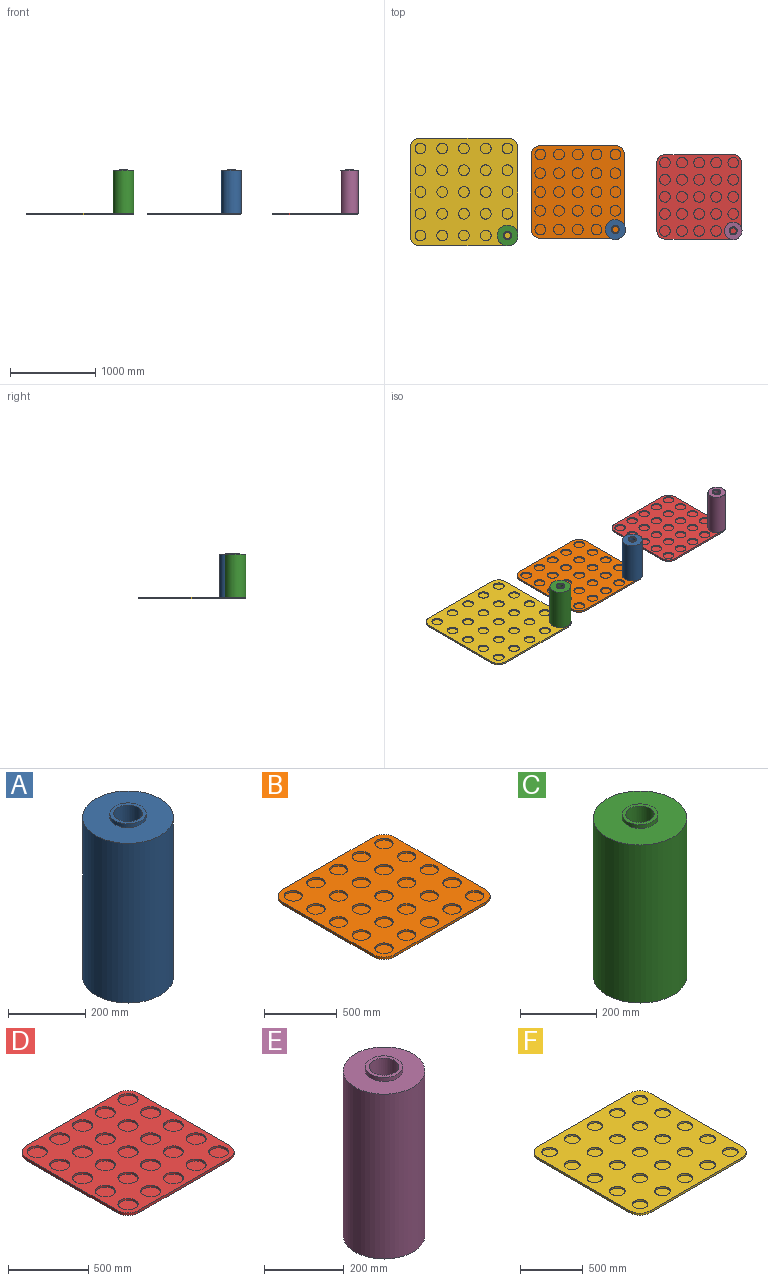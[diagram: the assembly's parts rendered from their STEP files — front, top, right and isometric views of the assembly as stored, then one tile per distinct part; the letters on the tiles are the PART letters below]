
ASSEMBLY  parts=6 mates=8
PART A: 8 faces, bbox 235x235x530 mm
  f0: cylinder r=117.5mm len=506mm, axis (0,0,-1), area 373566.8mm2, adj f3,f7
  f1: plane 94x94mm, normal (0,0,-1), area 2638.9mm2, adj f5,f6
  f2: cylinder r=47mm len=94mm, axis (0,0,1), area 3543.7mm2, adj f3,f4
  f3: plane 235x235mm, normal (0,0,1), area 36433.8mm2, adj f0,f2
  f4: plane 94x94mm, normal (0,0,1), area 2638.9mm2, adj f2,f5
  f5: cylinder r=37mm len=530mm, axis (0,0,1), area 123213.3mm2, adj f1,f4
  f6: cylinder r=47mm len=94mm, axis (0,0,-1), area 3543.7mm2, adj f1,f7
  f7: plane 235x235mm, normal (0,0,-1), area 36433.8mm2, adj f0,f6
PART B: 60 faces, bbox 1090x1090x20 mm
  f0: plane 1090x1090mm, normal (0,0,1), area 871839.9mm2, adj f1,f2,f3,f4,f5,f6,f7,f8
  f1: plane 880x20mm, normal (1,0,0), area 17600mm2, adj f0,f2,f8,f9
  f2: cylinder r=105mm len=105mm, axis (0,0,-1), area 3298.7mm2, adj f0,f1,f3,f9
  f3: plane 880x20mm, normal (0,1,0), area 17600mm2, adj f0,f2,f4,f9
  f4: cylinder r=105mm len=105mm, axis (0,0,-1), area 3298.7mm2, adj f0,f3,f5,f9
  f5: plane 880x20mm, normal (-1,0,0), area 17600mm2, adj f0,f4,f6,f9
  f6: cylinder r=105mm len=105mm, axis (0,0,-1), area 3298.7mm2, adj f0,f5,f7,f9
  f7: plane 880x20mm, normal (0,-1,0), area 17600mm2, adj f0,f6,f8,f9
  f8: cylinder r=105mm len=105mm, axis (0,0,-1), area 3298.7mm2, adj f0,f1,f7,f9
  f9: plane 1090x1090mm, normal (0,0,-1), area 1178636.1mm2, adj f1,f2,f3,f4,f5,f6,f7,f8
  f10: cylinder r=62.5mm len=125mm, axis (0,0,1), area 5890.5mm2, adj f0,f11
  f11: plane 125x125mm, normal (0,0,1), area 12271.8mm2, adj f10
  f12: cylinder r=62.5mm len=125mm, axis (0,0,1), area 5890.5mm2, adj f0,f13
  f13: plane 125x125mm, normal (0,0,1), area 12271.8mm2, adj f12
  f14: cylinder r=62.5mm len=125mm, axis (0,0,1), area 5890.5mm2, adj f0,f15
  f15: plane 125x125mm, normal (0,0,1), area 12271.8mm2, adj f14
  f16: cylinder r=62.5mm len=125mm, axis (0,0,1), area 5890.5mm2, adj f0,f17
  f17: plane 125x125mm, normal (0,0,1), area 12271.8mm2, adj f16
  f18: cylinder r=62.5mm len=125mm, axis (0,0,1), area 5890.5mm2, adj f0,f19
  f19: plane 125x125mm, normal (0,0,1), area 12271.8mm2, adj f18
  f20: cylinder r=62.5mm len=125mm, axis (0,0,1), area 5890.5mm2, adj f0,f21
  f21: plane 125x125mm, normal (0,0,1), area 12271.8mm2, adj f20
  f22: cylinder r=62.5mm len=125mm, axis (0,0,1), area 5890.5mm2, adj f0,f23
  f23: plane 125x125mm, normal (0,0,1), area 12271.8mm2, adj f22
  f24: cylinder r=62.5mm len=125mm, axis (0,0,1), area 5890.5mm2, adj f0,f25
  f25: plane 125x125mm, normal (0,0,1), area 12271.8mm2, adj f24
  f26: cylinder r=62.5mm len=125mm, axis (0,0,1), area 5890.5mm2, adj f0,f27
  f27: plane 125x125mm, normal (0,0,1), area 12271.8mm2, adj f26
  f28: cylinder r=62.5mm len=125mm, axis (0,0,1), area 5890.5mm2, adj f0,f29
  f29: plane 125x125mm, normal (0,0,1), area 12271.8mm2, adj f28
  f30: cylinder r=62.5mm len=125mm, axis (0,0,1), area 5890.5mm2, adj f0,f31
  f31: plane 125x125mm, normal (0,0,1), area 12271.8mm2, adj f30
  f32: cylinder r=62.5mm len=125mm, axis (0,0,1), area 5890.5mm2, adj f0,f33
  f33: plane 125x125mm, normal (0,0,1), area 12271.8mm2, adj f32
  f34: cylinder r=62.5mm len=125mm, axis (0,0,1), area 5890.5mm2, adj f0,f35
  f35: plane 125x125mm, normal (0,0,1), area 12271.8mm2, adj f34
  f36: cylinder r=62.5mm len=125mm, axis (0,0,1), area 5890.5mm2, adj f0,f37
  f37: plane 125x125mm, normal (0,0,1), area 12271.8mm2, adj f36
  f38: cylinder r=62.5mm len=125mm, axis (0,0,1), area 5890.5mm2, adj f0,f39
  f39: plane 125x125mm, normal (0,0,1), area 12271.8mm2, adj f38
  f40: cylinder r=62.5mm len=125mm, axis (0,0,1), area 5890.5mm2, adj f0,f41
  f41: plane 125x125mm, normal (0,0,1), area 12271.8mm2, adj f40
  f42: cylinder r=62.5mm len=125mm, axis (0,0,1), area 5890.5mm2, adj f0,f43
  f43: plane 125x125mm, normal (0,0,1), area 12271.8mm2, adj f42
  f44: cylinder r=62.5mm len=125mm, axis (0,0,1), area 5890.5mm2, adj f0,f45
  f45: plane 125x125mm, normal (0,0,1), area 12271.8mm2, adj f44
  f46: cylinder r=62.5mm len=125mm, axis (0,0,1), area 5890.5mm2, adj f0,f47
  f47: plane 125x125mm, normal (0,0,1), area 12271.8mm2, adj f46
  f48: cylinder r=62.5mm len=125mm, axis (0,0,1), area 5890.5mm2, adj f0,f49
  f49: plane 125x125mm, normal (0,0,1), area 12271.8mm2, adj f48
  f50: cylinder r=62.5mm len=125mm, axis (0,0,1), area 5890.5mm2, adj f0,f51
  f51: plane 125x125mm, normal (0,0,1), area 12271.8mm2, adj f50
  f52: cylinder r=62.5mm len=125mm, axis (0,0,1), area 5890.5mm2, adj f0,f53
  f53: plane 125x125mm, normal (0,0,1), area 12271.8mm2, adj f52
  f54: cylinder r=62.5mm len=125mm, axis (0,0,1), area 5890.5mm2, adj f0,f55
  f55: plane 125x125mm, normal (0,0,1), area 12271.8mm2, adj f54
  f56: cylinder r=62.5mm len=125mm, axis (0,0,1), area 5890.5mm2, adj f0,f57
  f57: plane 125x125mm, normal (0,0,1), area 12271.8mm2, adj f56
  f58: cylinder r=62.5mm len=125mm, axis (0,0,1), area 5890.5mm2, adj f0,f59
  f59: plane 125x125mm, normal (0,0,1), area 12271.8mm2, adj f58
PART C: 8 faces, bbox 245x245x530 mm
  f0: cylinder r=122.5mm len=506mm, axis (0,0,-1), area 389463.2mm2, adj f3,f7
  f1: plane 94x94mm, normal (0,0,-1), area 2638.9mm2, adj f5,f6
  f2: cylinder r=47mm len=94mm, axis (0,0,1), area 3543.7mm2, adj f3,f4
  f3: plane 245x245mm, normal (0,0,1), area 40203.7mm2, adj f0,f2
  f4: plane 94x94mm, normal (0,0,1), area 2638.9mm2, adj f2,f5
  f5: cylinder r=37mm len=530mm, axis (0,0,1), area 123213.3mm2, adj f1,f4
  f6: cylinder r=47mm len=94mm, axis (0,0,-1), area 3543.7mm2, adj f1,f7
  f7: plane 245x245mm, normal (0,0,-1), area 40203.7mm2, adj f0,f6
PART D: 60 faces, bbox 990x990x20 mm
  f0: plane 990x990mm, normal (0,0,1), area 665556.7mm2, adj f1,f2,f3,f4,f5,f6,f7,f8
  f1: plane 800x20mm, normal (1,0,0), area 16000mm2, adj f0,f2,f8,f9
  f2: cylinder r=95mm len=95mm, axis (0,0,-1), area 2984.5mm2, adj f0,f1,f3,f9
  f3: plane 800x20mm, normal (0,1,0), area 16000mm2, adj f0,f2,f4,f9
  f4: cylinder r=95mm len=95mm, axis (0,0,-1), area 2984.5mm2, adj f0,f3,f5,f9
  f5: plane 800x20mm, normal (-1,0,0), area 16000mm2, adj f0,f4,f6,f9
  f6: cylinder r=95mm len=95mm, axis (0,0,-1), area 2984.5mm2, adj f0,f5,f7,f9
  f7: plane 800x20mm, normal (0,-1,0), area 16000mm2, adj f0,f6,f8,f9
  f8: cylinder r=95mm len=95mm, axis (0,0,-1), area 2984.5mm2, adj f0,f1,f7,f9
  f9: plane 990x990mm, normal (0,0,-1), area 972352.9mm2, adj f1,f2,f3,f4,f5,f6,f7,f8
  f10: cylinder r=62.5mm len=125mm, axis (0,0,1), area 5890.5mm2, adj f0,f11
  f11: plane 125x125mm, normal (0,0,1), area 12271.8mm2, adj f10
  f12: cylinder r=62.5mm len=125mm, axis (0,0,1), area 5890.5mm2, adj f0,f13
  f13: plane 125x125mm, normal (0,0,1), area 12271.8mm2, adj f12
  f14: cylinder r=62.5mm len=125mm, axis (0,0,1), area 5890.5mm2, adj f0,f15
  f15: plane 125x125mm, normal (0,0,1), area 12271.8mm2, adj f14
  f16: cylinder r=62.5mm len=125mm, axis (0,0,1), area 5890.5mm2, adj f0,f17
  f17: plane 125x125mm, normal (0,0,1), area 12271.8mm2, adj f16
  f18: cylinder r=62.5mm len=125mm, axis (0,0,1), area 5890.5mm2, adj f0,f19
  f19: plane 125x125mm, normal (0,0,1), area 12271.8mm2, adj f18
  f20: cylinder r=62.5mm len=125mm, axis (0,0,1), area 5890.5mm2, adj f0,f21
  f21: plane 125x125mm, normal (0,0,1), area 12271.8mm2, adj f20
  f22: cylinder r=62.5mm len=125mm, axis (0,0,1), area 5890.5mm2, adj f0,f23
  f23: plane 125x125mm, normal (0,0,1), area 12271.8mm2, adj f22
  f24: cylinder r=62.5mm len=125mm, axis (0,0,1), area 5890.5mm2, adj f0,f25
  f25: plane 125x125mm, normal (0,0,1), area 12271.8mm2, adj f24
  f26: cylinder r=62.5mm len=125mm, axis (0,0,1), area 5890.5mm2, adj f0,f27
  f27: plane 125x125mm, normal (0,0,1), area 12271.8mm2, adj f26
  f28: cylinder r=62.5mm len=125mm, axis (0,0,1), area 5890.5mm2, adj f0,f29
  f29: plane 125x125mm, normal (0,0,1), area 12271.8mm2, adj f28
  f30: cylinder r=62.5mm len=125mm, axis (0,0,1), area 5890.5mm2, adj f0,f31
  f31: plane 125x125mm, normal (0,0,1), area 12271.8mm2, adj f30
  f32: cylinder r=62.5mm len=125mm, axis (0,0,1), area 5890.5mm2, adj f0,f33
  f33: plane 125x125mm, normal (0,0,1), area 12271.8mm2, adj f32
  f34: cylinder r=62.5mm len=125mm, axis (0,0,1), area 5890.5mm2, adj f0,f35
  f35: plane 125x125mm, normal (0,0,1), area 12271.8mm2, adj f34
  f36: cylinder r=62.5mm len=125mm, axis (0,0,1), area 5890.5mm2, adj f0,f37
  f37: plane 125x125mm, normal (0,0,1), area 12271.8mm2, adj f36
  f38: cylinder r=62.5mm len=125mm, axis (0,0,1), area 5890.5mm2, adj f0,f39
  f39: plane 125x125mm, normal (0,0,1), area 12271.8mm2, adj f38
  f40: cylinder r=62.5mm len=125mm, axis (0,0,1), area 5890.5mm2, adj f0,f41
  f41: plane 125x125mm, normal (0,0,1), area 12271.8mm2, adj f40
  f42: cylinder r=62.5mm len=125mm, axis (0,0,1), area 5890.5mm2, adj f0,f43
  f43: plane 125x125mm, normal (0,0,1), area 12271.8mm2, adj f42
  f44: cylinder r=62.5mm len=125mm, axis (0,0,1), area 5890.5mm2, adj f0,f45
  f45: plane 125x125mm, normal (0,0,1), area 12271.8mm2, adj f44
  f46: cylinder r=62.5mm len=125mm, axis (0,0,1), area 5890.5mm2, adj f0,f47
  f47: plane 125x125mm, normal (0,0,1), area 12271.8mm2, adj f46
  f48: cylinder r=62.5mm len=125mm, axis (0,0,1), area 5890.5mm2, adj f0,f49
  f49: plane 125x125mm, normal (0,0,1), area 12271.8mm2, adj f48
  f50: cylinder r=62.5mm len=125mm, axis (0,0,1), area 5890.5mm2, adj f0,f51
  f51: plane 125x125mm, normal (0,0,1), area 12271.8mm2, adj f50
  f52: cylinder r=62.5mm len=125mm, axis (0,0,1), area 5890.5mm2, adj f0,f53
  f53: plane 125x125mm, normal (0,0,1), area 12271.8mm2, adj f52
  f54: cylinder r=62.5mm len=125mm, axis (0,0,1), area 5890.5mm2, adj f0,f55
  f55: plane 125x125mm, normal (0,0,1), area 12271.8mm2, adj f54
  f56: cylinder r=62.5mm len=125mm, axis (0,0,1), area 5890.5mm2, adj f0,f57
  f57: plane 125x125mm, normal (0,0,1), area 12271.8mm2, adj f56
  f58: cylinder r=62.5mm len=125mm, axis (0,0,1), area 5890.5mm2, adj f0,f59
  f59: plane 125x125mm, normal (0,0,1), area 12271.8mm2, adj f58
PART E: 8 faces, bbox 205x205x530 mm
  f0: cylinder r=102.5mm len=506mm, axis (0,0,-1), area 325877.4mm2, adj f3,f7
  f1: plane 94x94mm, normal (0,0,-1), area 2638.9mm2, adj f5,f6
  f2: cylinder r=47mm len=94mm, axis (0,0,1), area 3543.7mm2, adj f3,f4
  f3: plane 205x205mm, normal (0,0,1), area 26066.6mm2, adj f0,f2
  f4: plane 94x94mm, normal (0,0,1), area 2638.9mm2, adj f2,f5
  f5: cylinder r=37mm len=530mm, axis (0,0,1), area 123213.3mm2, adj f1,f4
  f6: cylinder r=47mm len=94mm, axis (0,0,-1), area 3543.7mm2, adj f1,f7
  f7: plane 205x205mm, normal (0,0,-1), area 26066.6mm2, adj f0,f6
PART F: 60 faces, bbox 1265x1265x20 mm
  f0: plane 1265x1265mm, normal (0,0,1), area 1282076.4mm2, adj f1,f2,f3,f4,f5,f6,f7,f8
  f1: plane 1035x20mm, normal (1,0,0), area 20700mm2, adj f0,f2,f8,f9
  f2: cylinder r=115mm len=115mm, axis (0,0,-1), area 3612.8mm2, adj f0,f1,f3,f9
  f3: plane 1035x20mm, normal (0,1,0), area 20700mm2, adj f0,f2,f4,f9
  f4: cylinder r=115mm len=115mm, axis (0,0,-1), area 3612.8mm2, adj f0,f3,f5,f9
  f5: plane 1035x20mm, normal (-1,0,0), area 20700mm2, adj f0,f4,f6,f9
  f6: cylinder r=115mm len=115mm, axis (0,0,-1), area 3612.8mm2, adj f0,f5,f7,f9
  f7: plane 1035x20mm, normal (0,-1,0), area 20700mm2, adj f0,f6,f8,f9
  f8: cylinder r=115mm len=115mm, axis (0,0,-1), area 3612.8mm2, adj f0,f1,f7,f9
  f9: plane 1265x1265mm, normal (0,0,-1), area 1588872.6mm2, adj f1,f2,f3,f4,f5,f6,f7,f8
  f10: cylinder r=62.5mm len=125mm, axis (0,0,1), area 5890.5mm2, adj f0,f11
  f11: plane 125x125mm, normal (0,0,1), area 12271.8mm2, adj f10
  f12: cylinder r=62.5mm len=125mm, axis (0,0,1), area 5890.5mm2, adj f0,f13
  f13: plane 125x125mm, normal (0,0,1), area 12271.8mm2, adj f12
  f14: cylinder r=62.5mm len=125mm, axis (0,0,1), area 5890.5mm2, adj f0,f15
  f15: plane 125x125mm, normal (0,0,1), area 12271.8mm2, adj f14
  f16: cylinder r=62.5mm len=125mm, axis (0,0,1), area 5890.5mm2, adj f0,f17
  f17: plane 125x125mm, normal (0,0,1), area 12271.8mm2, adj f16
  f18: cylinder r=62.5mm len=125mm, axis (0,0,1), area 5890.5mm2, adj f0,f19
  f19: plane 125x125mm, normal (0,0,1), area 12271.8mm2, adj f18
  f20: cylinder r=62.5mm len=125mm, axis (0,0,1), area 5890.5mm2, adj f0,f21
  f21: plane 125x125mm, normal (0,0,1), area 12271.8mm2, adj f20
  f22: cylinder r=62.5mm len=125mm, axis (0,0,1), area 5890.5mm2, adj f0,f23
  f23: plane 125x125mm, normal (0,0,1), area 12271.8mm2, adj f22
  f24: cylinder r=62.5mm len=125mm, axis (0,0,1), area 5890.5mm2, adj f0,f25
  f25: plane 125x125mm, normal (0,0,1), area 12271.8mm2, adj f24
  f26: cylinder r=62.5mm len=125mm, axis (0,0,1), area 5890.5mm2, adj f0,f27
  f27: plane 125x125mm, normal (0,0,1), area 12271.8mm2, adj f26
  f28: cylinder r=62.5mm len=125mm, axis (0,0,1), area 5890.5mm2, adj f0,f29
  f29: plane 125x125mm, normal (0,0,1), area 12271.8mm2, adj f28
  f30: cylinder r=62.5mm len=125mm, axis (0,0,1), area 5890.5mm2, adj f0,f31
  f31: plane 125x125mm, normal (0,0,1), area 12271.8mm2, adj f30
  f32: cylinder r=62.5mm len=125mm, axis (0,0,1), area 5890.5mm2, adj f0,f33
  f33: plane 125x125mm, normal (0,0,1), area 12271.8mm2, adj f32
  f34: cylinder r=62.5mm len=125mm, axis (0,0,1), area 5890.5mm2, adj f0,f35
  f35: plane 125x125mm, normal (0,0,1), area 12271.8mm2, adj f34
  f36: cylinder r=62.5mm len=125mm, axis (0,0,1), area 5890.5mm2, adj f0,f37
  f37: plane 125x125mm, normal (0,0,1), area 12271.8mm2, adj f36
  f38: cylinder r=62.5mm len=125mm, axis (0,0,1), area 5890.5mm2, adj f0,f39
  f39: plane 125x125mm, normal (0,0,1), area 12271.8mm2, adj f38
  f40: cylinder r=62.5mm len=125mm, axis (0,0,1), area 5890.5mm2, adj f0,f41
  f41: plane 125x125mm, normal (0,0,1), area 12271.8mm2, adj f40
  f42: cylinder r=62.5mm len=125mm, axis (0,0,1), area 5890.5mm2, adj f0,f43
  f43: plane 125x125mm, normal (0,0,1), area 12271.8mm2, adj f42
  f44: cylinder r=62.5mm len=125mm, axis (0,0,1), area 5890.5mm2, adj f0,f45
  f45: plane 125x125mm, normal (0,0,1), area 12271.8mm2, adj f44
  f46: cylinder r=62.5mm len=125mm, axis (0,0,1), area 5890.5mm2, adj f0,f47
  f47: plane 125x125mm, normal (0,0,1), area 12271.8mm2, adj f46
  f48: cylinder r=62.5mm len=125mm, axis (0,0,1), area 5890.5mm2, adj f0,f49
  f49: plane 125x125mm, normal (0,0,1), area 12271.8mm2, adj f48
  f50: cylinder r=62.5mm len=125mm, axis (0,0,1), area 5890.5mm2, adj f0,f51
  f51: plane 125x125mm, normal (0,0,1), area 12271.8mm2, adj f50
  f52: cylinder r=62.5mm len=125mm, axis (0,0,1), area 5890.5mm2, adj f0,f53
  f53: plane 125x125mm, normal (0,0,1), area 12271.8mm2, adj f52
  f54: cylinder r=62.5mm len=125mm, axis (0,0,1), area 5890.5mm2, adj f0,f55
  f55: plane 125x125mm, normal (0,0,1), area 12271.8mm2, adj f54
  f56: cylinder r=62.5mm len=125mm, axis (0,0,1), area 5890.5mm2, adj f0,f57
  f57: plane 125x125mm, normal (0,0,1), area 12271.8mm2, adj f56
  f58: cylinder r=62.5mm len=125mm, axis (0,0,1), area 5890.5mm2, adj f0,f59
  f59: plane 125x125mm, normal (0,0,1), area 12271.8mm2, adj f58
PLACE A t=(1773.53,-440,8)mm
PLACE B t=(1333.53,0,0)mm
PLACE C t=(510,-510,8)mm
PLACE D t=(2754.56,-56.28,0)mm
PLACE E t=(3154.56,-456.28,8)mm
PLACE F at identity
MATE planar F.f52 <-> C.f0  axis (0,0,1) through (255,0,20)mm
MATE planar D.f8 <-> E.f0  axis (0,0,1) through (3154.56,-456.28,20)mm
MATE cylindrical A.f0 <-> B.f8  axis (0,0,-1) through (1773.53,-440,20)mm
MATE planar D.f9 <-> F.f50  axis (0,0,-1) through (2354.56,-551.28,0)mm
MATE cylindrical D.f8 <-> E.f6  axis (0,0,1) through (3154.56,-456.28,20)mm
MATE planar B.f50 <-> F.f50  axis (0,0,-1) through (1333.53,0,0)mm
MATE planar A.f0 <-> B.f50  axis (0,0,-1) through (1773.53,-440,20)mm
MATE cylindrical F.f26 <-> C.f6  axis (0,0,1) through (510,-510,12.5)mm
